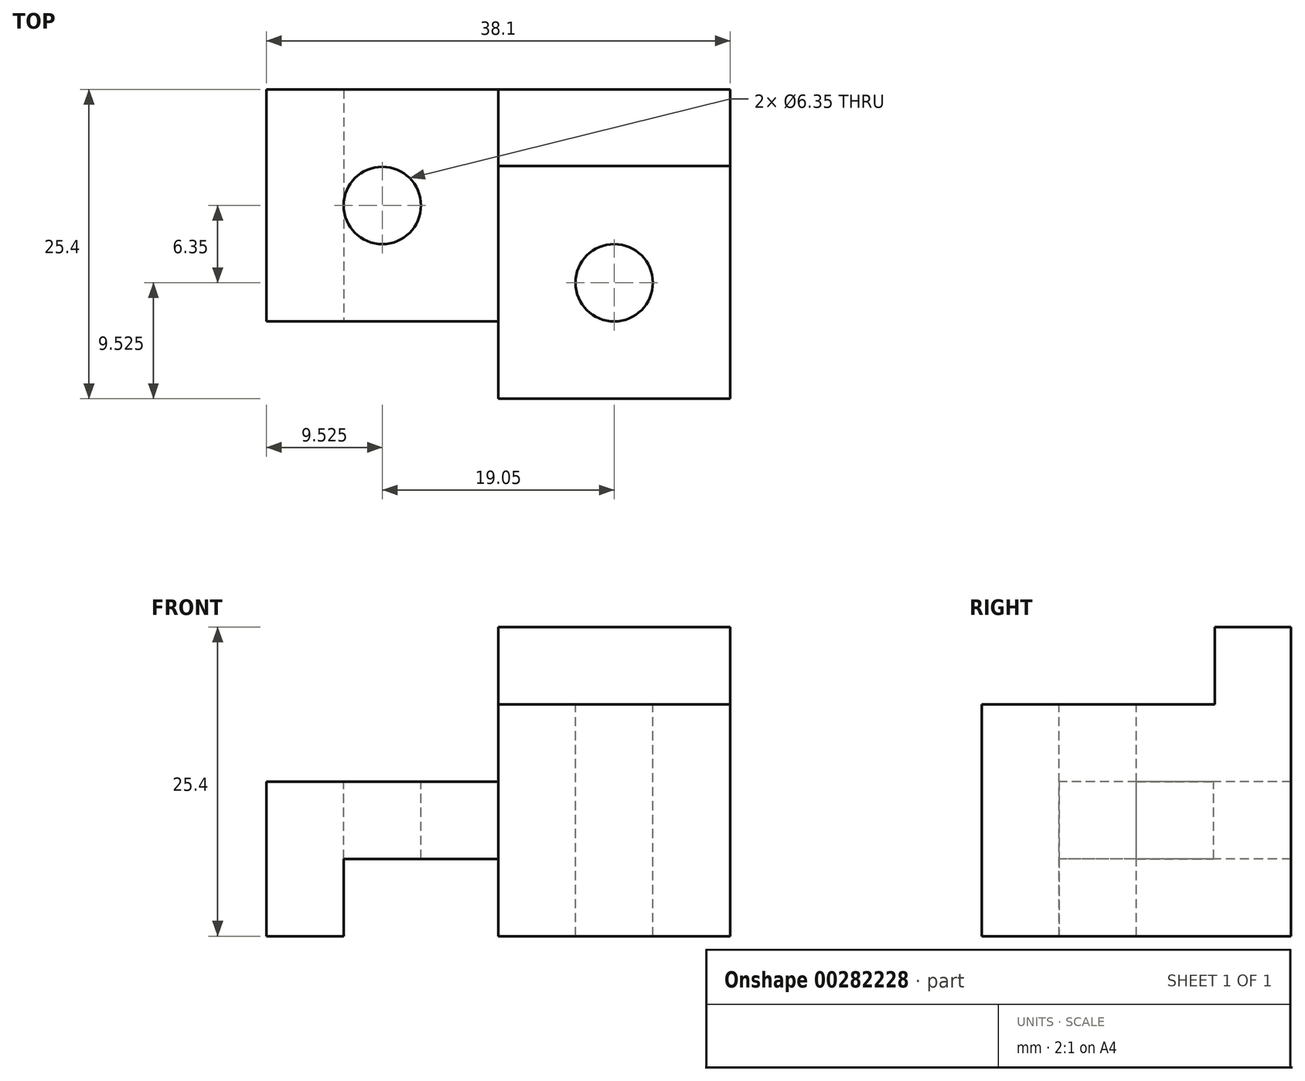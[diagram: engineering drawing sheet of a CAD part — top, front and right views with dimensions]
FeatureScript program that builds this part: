
annotation { "Feature Type Name" : "Feature", "Feature Type Description" : "" }
export const myFeature = defineFeature(function(context is Context, id is Id, definition is map)
    precondition{}
    {
        {
            var Q0;
            Q0=qCreatedBy(makeId("Front.planeOp"),FACE);
            var sketch = newSketch(context, id + "F0", { "sketchPlane" : qUnion([Q0])});
            skLineSegment(sketch, "E0", {"start": v(0, 0) * mm, "end": v(0, 12.7) * mm});
            skLineSegment(sketch, "E1", {"start": v(0, 12.7) * mm, "end": v(19.05, 12.7) * mm});
            skLineSegment(sketch, "E2", {"start": v(19.05, 12.7) * mm, "end": v(19.05, 6.35) * mm});
            skLineSegment(sketch, "E3", {"start": v(19.05, 6.35) * mm, "end": v(6.35, 6.35) * mm});
            skLineSegment(sketch, "E4", {"start": v(6.35, 6.35) * mm, "end": v(6.35, 0) * mm});
            skLineSegment(sketch, "E5", {"start": v(6.35, 0) * mm, "end": v(0, 0) * mm});
            skSolve(sketch);
        }
        {
            var Q0;
            Q0=makeQuery(id+"F0.imprint","IMPRINT",FACE,{"disambiguationData":[TD([[makeQuery(id+"F0.imprint","IMPRINT",EDGE,{"derivedFrom":sQuery(id+"F0.wireOp",EDGE,"E0")}),-1.0]])]});
            extrude(context, id + "F1", {"entities" : qUnion([Q0]), "oppositeDirection" : true, "depth" : 19.05 * mm});
        }
        {
            var Q0;
            Q0=qCreatedBy(makeId("Top.planeOp"),FACE);
            var sketch = newSketch(context, id + "F2", { "sketchPlane" : qUnion([Q0])});
            skLineSegment(sketch, "E6.bottom", {"start": v(19.05, 19.05) * mm, "end": v(38.1, 19.05) * mm});
            skLineSegment(sketch, "E6.top", {"start": v(19.05, -6.35) * mm, "end": v(38.1, -6.35) * mm});
            skLineSegment(sketch, "E6.left", {"start": v(19.05, 19.05) * mm, "end": v(19.05, -6.35) * mm});
            skLineSegment(sketch, "E6.right", {"start": v(38.1, 19.05) * mm, "end": v(38.1, -6.35) * mm});
            skSolve(sketch);
        }
        {
            var Q0;
            Q0=makeQuery(id+"F2.imprint","IMPRINT",FACE,{"disambiguationData":[TD([[makeQuery(id+"F2.imprint","IMPRINT",EDGE,{"derivedFrom":sQuery(id+"F2.wireOp",EDGE,"E6.bottom")}),-1.0]])]});
            extrude(context, id + "F3", {"entities" : qUnion([Q0]), "operationType" : NewBodyOperationType.ADD, "depth" : 25.4 * mm});
        }
        {
            var Q0;
            Q0=makeQuery(id+"F3.opExtrude","CAP_FACE",FACE,{"disambiguationData":[OSD([sQuery(id+"F2.wireOp",EDGE,"E6.bottom"),sQuery(id+"F2.wireOp",EDGE,"E6.top"),sQuery(id+"F2.wireOp",EDGE,"E6.left"),sQuery(id+"F2.wireOp",EDGE,"E6.right")])],"isStart":false});
            var sketch = newSketch(context, id + "F4", { "sketchPlane" : qUnion([Q0])});
            skLineSegment(sketch, "E7.bottom", {"start": v(19.05, 12.78) * mm, "end": v(38.1, 12.78) * mm});
            skLineSegment(sketch, "E7.top", {"start": v(19.05, -6.35) * mm, "end": v(38.1, -6.35) * mm});
            skLineSegment(sketch, "E7.left", {"start": v(19.05, 12.78) * mm, "end": v(19.05, -6.35) * mm});
            skLineSegment(sketch, "E7.right", {"start": v(38.1, 12.78) * mm, "end": v(38.1, -6.35) * mm});
            skSolve(sketch);
        }
        {
            var Q0;
            Q0=makeQuery(id+"F4.imprint","IMPRINT",FACE,{"disambiguationData":[TD([[makeQuery(id+"F4.imprint","IMPRINT",EDGE,{"derivedFrom":sQuery(id+"F4.wireOp",EDGE,"E7.bottom")}),-1.0]])]});
            extrude(context, id + "F5", {"entities" : qUnion([Q0]), "operationType" : NewBodyOperationType.REMOVE, "oppositeDirection" : true, "depth" : 6.35 * mm});
        }
        {
            var Q0;
            Q0=makeQuery(id+"F1.opExtrude","SWEPT_FACE",FACE,{"disambiguationData":[OSD([sQuery(id+"F0.wireOp",EDGE,"E1")])]});
            var sketch = newSketch(context, id + "F6", { "sketchPlane" : qUnion([Q0])});
            skCircle(sketch, "E8", {"center": v(9.52, 9.53) * mm, "radius": 3.18 * mm});
            skCircle(sketch, "E9", {"center": v(28.57, 3.17) * mm, "radius": 3.18 * mm});
            skSolve(sketch);
        }
        {
            var Q0;
            Q0=makeQuery(id+"F6.imprint","IMPRINT",FACE,{"disambiguationData":[TD([[makeQuery(id+"F6.imprint","IMPRINT",EDGE,{"derivedFrom":sQuery(id+"F6.wireOp",EDGE,"E9")}),1.0]])]});
            var Q1;
            Q1=makeQuery(id+"F6.imprint","IMPRINT",FACE,{"disambiguationData":[TD([[makeQuery(id+"F6.imprint","IMPRINT",EDGE,{"derivedFrom":sQuery(id+"F6.wireOp",EDGE,"E8")}),1.0]])]});
            extrude(context, id + "F7", {"entities" : qUnion([Q0, Q1]), "operationType" : NewBodyOperationType.REMOVE, "endBound" : BoundingType.SYMMETRIC, "oppositeDirection" : true, "depth" : 25.4 * mm});
        }
    });
